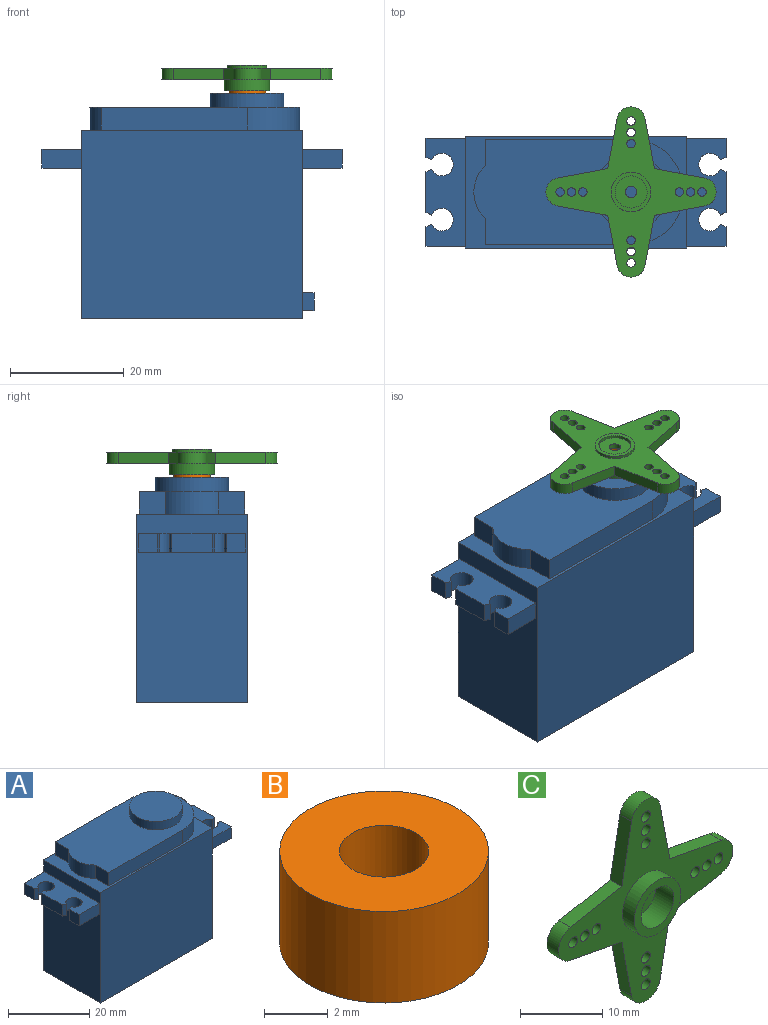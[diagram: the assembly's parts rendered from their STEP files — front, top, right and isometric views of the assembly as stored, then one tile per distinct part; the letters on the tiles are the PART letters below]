
ASSEMBLY  parts=3 mates=2
PART A: 46 faces, bbox 52.9x19.7x39.7 mm
  f0: plane 7.16x3.34mm, normal (1,0,0), area 23.9mm2, adj f4,f5,f39,f42
  f1: plane 3.38x3.34mm, normal (1,0,0), area 11.3mm2, adj f4,f5,f16,f38
  f2: plane 3.38x3.34mm, normal (-1,0,0), area 11.3mm2, adj f6,f7,f18,f35
  f3: plane 7.16x3.34mm, normal (-1,0,0), area 23.9mm2, adj f6,f7,f34,f37
  f4: plane 19x6.93mm, normal (0,0,-1), area 102.8mm2, adj f0,f1,f10,f14,f15,f16,f38,f39
  f5: plane 19x6.93mm, normal (0,0,1), area 102.8mm2, adj f0,f1,f10,f14,f15,f16,f38,f39
  f6: plane 19x6.93mm, normal (0,0,1), area 102.8mm2, adj f2,f3,f8,f17,f18,f19,f32,f33
  f7: plane 19x6.93mm, normal (0,0,-1), area 102.8mm2, adj f2,f3,f8,f17,f18,f19,f32,f33
  f8: plane 33.2x19.7mm, normal (-1,0,0), area 590.6mm2, adj f6,f7,f9,f11,f12,f13,f18,f19
  f9: plane 39x19.7mm, normal (0,0,-1), area 768.3mm2, adj f8,f10,f12,f13
  f10: plane 33.2x19.7mm, normal (1,0,0), area 570.4mm2, adj f4,f5,f9,f11,f12,f13,f15,f16
  f11: plane 39x19.7mm, normal (0,0,1), area 141.5mm2, adj f8,f10,f12,f13,f25,f26,f27,f28
  f12: plane 39x33.2mm, normal (0,-1,0), area 1294.8mm2, adj f8,f9,f10,f11
  f13: plane 39x33.2mm, normal (0,1,0), area 1294.8mm2, adj f8,f9,f10,f11
  f14: plane 3.38x3.34mm, normal (1,0,0), area 11.3mm2, adj f4,f5,f15,f41
  f15: plane 6.93x3.34mm, normal (0,1,0), area 23.1mm2, adj f4,f5,f10,f14
  f16: plane 6.93x3.34mm, normal (0,-1,0), area 23.1mm2, adj f1,f4,f5,f10
  f17: plane 3.38x3.34mm, normal (-1,0,0), area 11.3mm2, adj f6,f7,f19,f33
  f18: plane 6.93x3.34mm, normal (0,-1,0), area 23.1mm2, adj f2,f6,f7,f8
  f19: plane 6.93x3.34mm, normal (0,1,0), area 23.1mm2, adj f6,f7,f8,f17
  f20: plane 6.4x2mm, normal (0,0,1), area 12.8mm2, adj f10,f21,f23,f24
  f21: plane 3.15x2mm, normal (0,-1,0), area 6.3mm2, adj f10,f20,f22,f24
  f22: plane 6.4x2mm, normal (0,0,-1), area 12.8mm2, adj f10,f21,f23,f24
  f23: plane 3.15x2mm, normal (0,1,0), area 6.3mm2, adj f10,f20,f22,f24
  f24: plane 6.4x3.15mm, normal (1,0,0), area 20.2mm2, adj f20,f21,f22,f23
  f25: plane 4.61x4mm, normal (-1,0,0), area 18.4mm2, adj f11,f26,f30,f31
  f26: cylinder r=6.5mm len=9.38mm, axis (0,0,-1), area 41.9mm2, adj f11,f25,f27,f31
  f27: plane 4.61x4mm, normal (-1,0,0), area 18.4mm2, adj f11,f26,f28,f31
  f28: plane 25.7x4mm, normal (0,-1,0), area 102.8mm2, adj f11,f27,f29,f31
  f29: cylinder r=9.3mm len=18.6mm, axis (0,0,-1), area 116.9mm2, adj f11,f28,f30,f31
  f30: plane 25.7x4mm, normal (0,1,0), area 102.8mm2, adj f11,f25,f29,f31
  f31: plane 37x18.6mm, normal (0,0,1), area 494.1mm2, adj f25,f26,f27,f28,f29,f30,f44
  f32: cylinder r=2mm len=4mm, axis (0,0,1), area 36.3mm2, adj f6,f7,f33,f34
  f33: plane 3.34x0.98mm, normal (-0.41,-0.91,0), area 3.6mm2, adj f6,f7,f17,f32
  f34: plane 3.34x0.98mm, normal (-0.41,0.91,0), area 3.6mm2, adj f3,f6,f7,f32
  f35: plane 3.34x0.98mm, normal (-0.41,0.91,0), area 3.6mm2, adj f2,f6,f7,f36
  f36: cylinder r=2mm len=4mm, axis (0,0,1), area 36.3mm2, adj f6,f7,f35,f37
  f37: plane 3.34x0.98mm, normal (-0.41,-0.91,0), area 3.6mm2, adj f3,f6,f7,f36
  f38: plane 3.34x0.98mm, normal (0.41,0.91,0), area 3.6mm2, adj f1,f4,f5,f40
  f39: plane 3.34x0.98mm, normal (0.41,-0.91,0), area 3.6mm2, adj f0,f4,f5,f40
  f40: cylinder r=2mm len=4mm, axis (0,0,1), area 36.3mm2, adj f4,f5,f38,f39
  f41: plane 3.34x0.98mm, normal (0.41,-0.91,0), area 3.6mm2, adj f4,f5,f14,f43
  f42: plane 3.34x0.98mm, normal (0.41,0.91,0), area 3.6mm2, adj f0,f4,f5,f43
  f43: cylinder r=2mm len=4mm, axis (0,0,1), area 36.3mm2, adj f4,f5,f41,f42
  f44: cylinder r=6.5mm len=13mm, axis (0,0,-1), area 102.1mm2, adj f31,f45
  f45: plane 13x13mm, normal (0,0,1), area 132.7mm2, adj f44
PART B: 4 faces, bbox 6.5x6.5x3.5 mm
  f0: cylinder r=3.27mm len=6.53mm, axis (0,0,-1), area 71.8mm2, adj f1,f2
  f1: plane 6.53x6.53mm, normal (0,0,1), area 27.4mm2, adj f0,f3
  f2: plane 6.53x6.53mm, normal (0,0,-1), area 27.4mm2, adj f0,f3
  f3: cylinder r=1.4mm len=3.5mm, axis (0,0,1), area 30.7mm2, adj f1,f2
PART C: 35 faces, bbox 30x4.5x30 mm
  f0: cylinder r=2.5mm len=4.91mm, axis (0,1,0), area 13.8mm2, adj f1,f23,f24,f25
  f1: plane 8.84x2mm, normal (-0.18,0,-0.98), area 18mm2, adj f0,f2,f24,f25
  f2: plane 8.84x2mm, normal (-0.98,0,-0.18), area 18mm2, adj f1,f3,f24,f25
  f3: cylinder r=2.5mm len=4.91mm, axis (0,1,0), area 13.8mm2, adj f2,f4,f24,f25
  f4: plane 8.84x2mm, normal (0.98,0,-0.18), area 18mm2, adj f3,f5,f24,f25
  f5: plane 8.84x2mm, normal (0.18,0,-0.98), area 18mm2, adj f4,f6,f24,f25
  f6: cylinder r=2.5mm len=4.91mm, axis (0,1,0), area 13.8mm2, adj f5,f7,f24,f25
  f7: plane 8.84x2mm, normal (0.18,0,0.98), area 18mm2, adj f6,f8,f24,f25
  f8: plane 8.84x2mm, normal (0.98,0,0.18), area 18mm2, adj f7,f9,f24,f25
  f9: cylinder r=2.5mm len=4.91mm, axis (0,1,0), area 13.8mm2, adj f8,f10,f24,f25
  f10: plane 8.84x2mm, normal (-0.98,0,0.18), area 18mm2, adj f9,f23,f24,f25
  f11: cylinder r=0.75mm len=2mm, axis (0,1,0), area 9.4mm2, adj f24,f25
  f12: cylinder r=0.75mm len=2mm, axis (0,1,0), area 9.4mm2, adj f24,f25
  f13: cylinder r=0.75mm len=2mm, axis (0,1,0), area 9.4mm2, adj f24,f25
  f14: cylinder r=0.75mm len=2mm, axis (0,1,0), area 9.4mm2, adj f24,f25
  f15: cylinder r=0.75mm len=2mm, axis (0,1,0), area 9.4mm2, adj f24,f25
  f16: cylinder r=0.75mm len=2mm, axis (0,1,0), area 9.4mm2, adj f24,f25
  f17: cylinder r=0.75mm len=2mm, axis (0,1,0), area 9.4mm2, adj f24,f25
  f18: cylinder r=0.75mm len=2mm, axis (0,1,0), area 9.4mm2, adj f24,f25
  f19: cylinder r=0.75mm len=2mm, axis (0,1,0), area 9.4mm2, adj f24,f25
  f20: cylinder r=0.75mm len=2mm, axis (0,1,0), area 9.4mm2, adj f24,f25
  f21: cylinder r=0.75mm len=2mm, axis (0,1,0), area 9.4mm2, adj f24,f25
  f22: cylinder r=0.75mm len=2mm, axis (0,1,0), area 9.4mm2, adj f24,f25
  f23: plane 8.84x2mm, normal (-0.18,0,0.98), area 18mm2, adj f0,f10,f24,f25
  f24: plane 30x30mm, normal (0,-1,0), area 259.1mm2, adj f0,f1,f2,f3,f4,f5,f6,f7
  f25: plane 30x30mm, normal (0,1,0), area 270.9mm2, adj f0,f1,f2,f3,f4,f5,f6,f7
  f26: cylinder r=4mm len=8mm, axis (0,1,0), area 50.3mm2, adj f24,f27
  f27: plane 8x8mm, normal (0,-1,0), area 25.2mm2, adj f26,f28
  f28: cylinder r=2.82mm len=5.65mm, axis (0,-1,0), area 55mm2, adj f27,f29
  f29: plane 5.65x5.65mm, normal (0,-1,0), area 21.9mm2, adj f28,f34
  f30: cylinder r=3.5mm len=7mm, axis (0,-1,0), area 11mm2, adj f25,f31
  f31: plane 7x7mm, normal (0,1,0), area 13.4mm2, adj f30,f32
  f32: cylinder r=2.82mm len=5.65mm, axis (0,1,0), area 8.9mm2, adj f31,f33
  f33: plane 5.65x5.65mm, normal (0,1,0), area 21.9mm2, adj f32,f34
  f34: cylinder r=1mm len=2mm, axis (0,-1,0), area 5.7mm2, adj f29,f33
PLACE A at identity fixed
PLACE B at identity
PLACE C rot(axis=(1,0,0),90deg) t=(0,0,17.6)mm
MATE fastened C.f28 <-> B.f3  axis (0,0,-1) through (0,0,16.7)mm
MATE revolute A.f29 <-> B.f0  axis (0,0,1) through (0,0,13.2)mm
